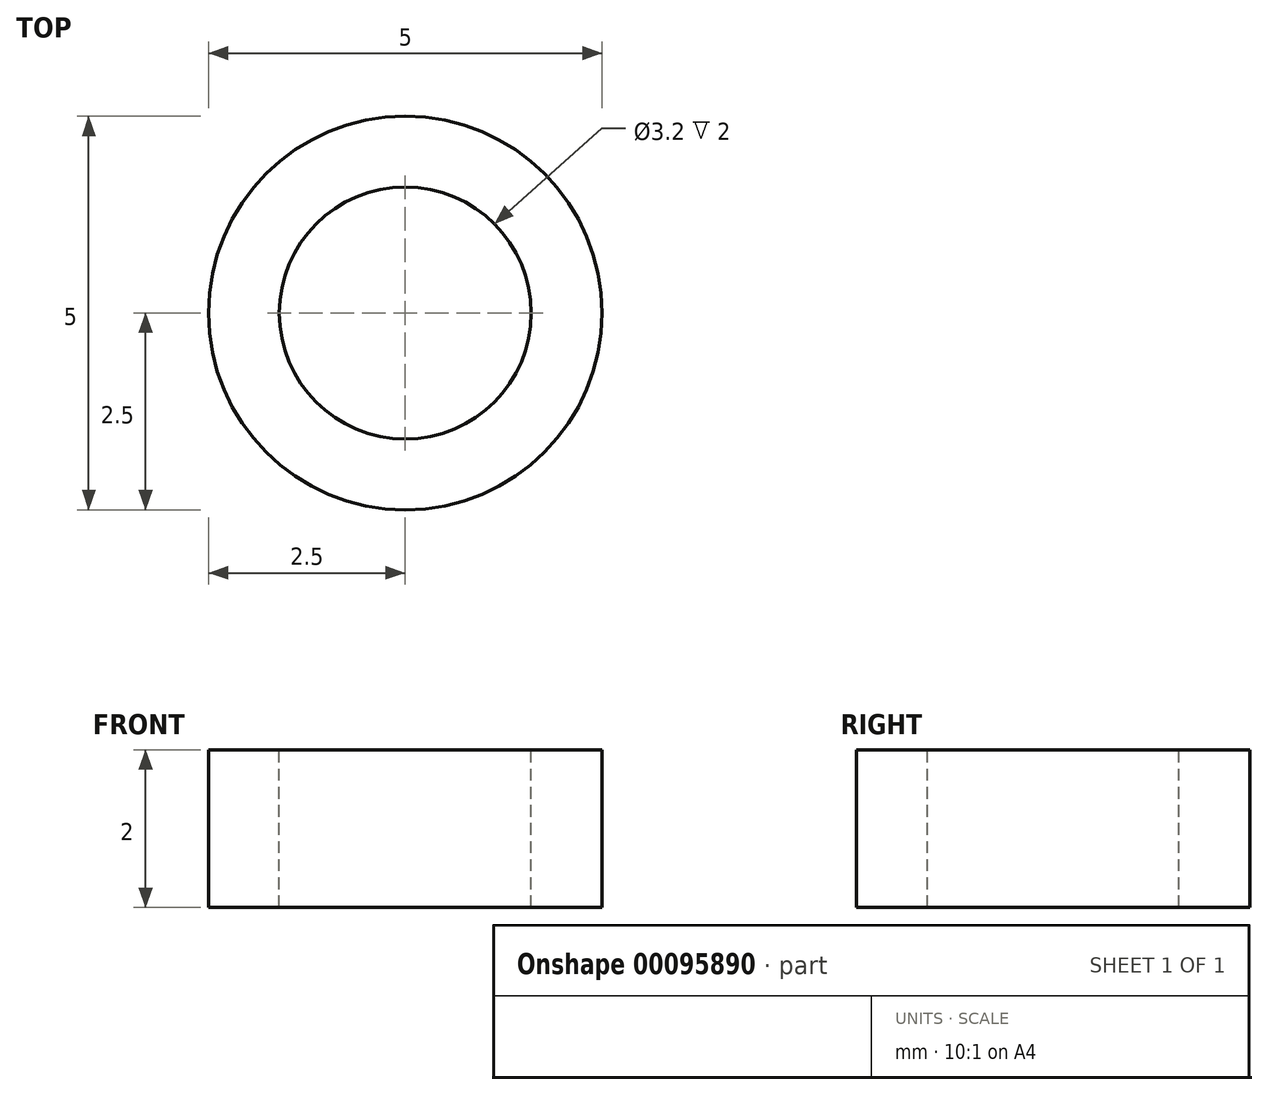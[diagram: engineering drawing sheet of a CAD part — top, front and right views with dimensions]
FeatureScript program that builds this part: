
annotation { "Feature Type Name" : "Feature", "Feature Type Description" : "" }
export const myFeature = defineFeature(function(context is Context, id is Id, definition is map)
    precondition{}
    {
        {
            var Q0;
            Q0=qCreatedBy(makeId("Front.planeOp"),FACE);
            var sketch = newSketch(context, id + "F0", { "sketchPlane" : qUnion([Q0])});
            skLineSegment(sketch, "E0", {"start": v(0, 0) * mm, "end": v(0, 2) * mm});
            skLineSegment(sketch, "E1", {"start": v(0, 2) * mm, "end": v(2.5, 2) * mm});
            skLineSegment(sketch, "E2", {"start": v(2.5, 2) * mm, "end": v(2.5, 0) * mm});
            skLineSegment(sketch, "E3", {"start": v(2.5, 0) * mm, "end": v(0, 0) * mm});
            skSolve(sketch);
        }
        {
            var Q0;
            Q0=makeQuery(id+"F0.imprint","IMPRINT",FACE,{"disambiguationData":[TD([[makeQuery(id+"F0.imprint","IMPRINT",EDGE,{"derivedFrom":sQuery(id+"F0.wireOp",EDGE,"E0")}),-1.0]])]});
            var Q1;
            Q1=sQuery(id+"F0.wireOp",EDGE,"E0");
            revolve(context, id + "F1", {"entities" : qUnion([Q0]), "axis" : qUnion([Q1]), "revolveType" : RevolveType.FULL});
        }
        {
            var Q0;
            Q0=makeQuery(id+"F1.opRevolve","SWEPT_FACE",FACE,{"disambiguationData":[OSD([sQuery(id+"F0.wireOp",EDGE,"E1")])]});
            var sketch = newSketch(context, id + "F2", { "sketchPlane" : qUnion([Q0])});
            skCircle(sketch, "E4", {"center": v(0, 0) * mm, "radius": 1.6 * mm});
            skSolve(sketch);
        }
        {
            var Q0;
            Q0=makeQuery(id+"F2.imprint","IMPRINT",FACE,{"disambiguationData":[TD([[makeQuery(id+"F2.imprint","IMPRINT",EDGE,{"derivedFrom":sQuery(id+"F2.wireOp",EDGE,"E4")}),1.0]])]});
            extrude(context, id + "F3", {"entities" : qUnion([Q0]), "operationType" : NewBodyOperationType.REMOVE, "oppositeDirection" : true, "depth" : 3 * mm});
        }
    });
